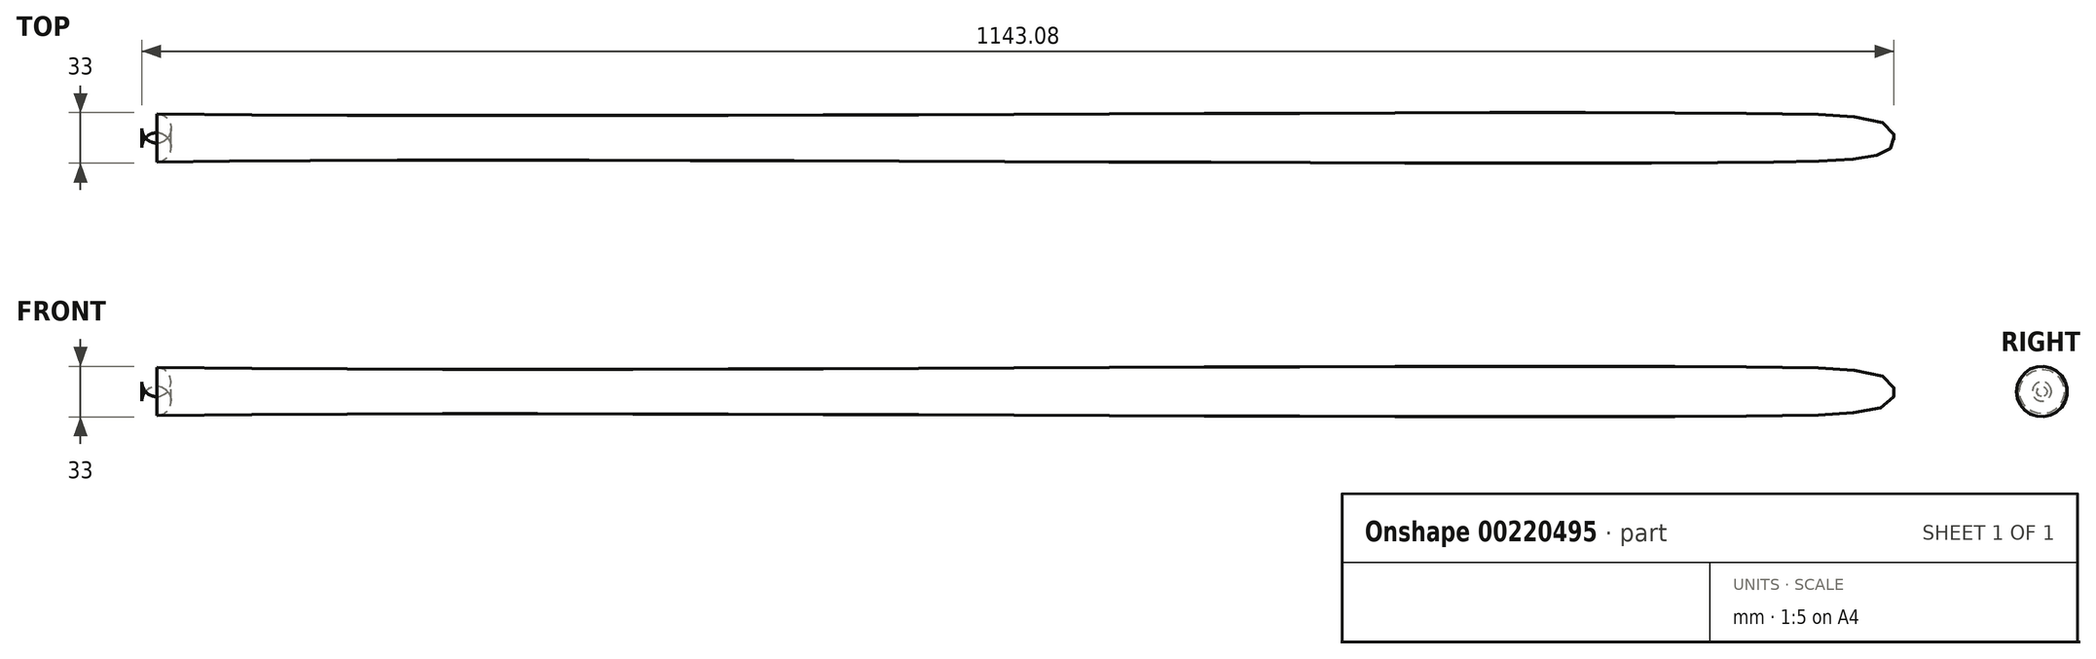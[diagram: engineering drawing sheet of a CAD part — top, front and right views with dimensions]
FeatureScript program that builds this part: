
annotation { "Feature Type Name" : "Feature", "Feature Type Description" : "" }
export const myFeature = defineFeature(function(context is Context, id is Id, definition is map)
    precondition{}
    {
        {
            var Q0;
            Q0=qCreatedBy(makeId("Top.planeOp"),FACE);
            var sketch = newSketch(context, id + "F0", { "sketchPlane" : qUnion([Q0])});
            skLineSegment(sketch, "E0", {"start": v(-571.5, 0) * mm, "end": v(571.5, 0) * mm});
            skLineSegment(sketch, "E1", {"start": v(-571.5, 0) * mm, "end": v(-571.5, -15.88) * mm});
            skFitSpline(sketch, "E2", {"points": [v(-571.5, -15.88) * mm, v(493.28, -15.87) * mm, v(571.5, 0) * mm], "startDerivative": vector(1003.6, 15.39) * mm, "endDerivative": vector(-23.38, 192.15) * mm});
            skSolve(sketch);
        }
        {
            var Q0;
            Q0=makeQuery(id+"F0.imprint","IMPRINT",FACE,{"disambiguationData":[TD([[makeQuery(id+"F0.imprint","IMPRINT",EDGE,{"derivedFrom":sQuery(id+"F0.wireOp",EDGE,"E0")}),-1.0]])]});
            var Q1;
            Q1=sQuery(id+"F0.wireOp",EDGE,"E0");
            revolve(context, id + "F1", {"entities" : qUnion([Q0]), "axis" : qUnion([Q1]), "revolveType" : RevolveType.FULL});
        }
        {
            var Q0;
            Q0=makeQuery(id+"F1.opRevolve","SWEPT_EDGE",EDGE,{"disambiguationData":[OSD([sQuery(id+"F0.wireOp",EDGE,"E1"),sQuery(id+"F0.wireOp",EDGE,"E2")])]});
            fillet(context, id + "F2", {"entities" : qUnion([Q0]), "radius" : 9.52 * mm, "tangentPropagation" : true, "allowEdgeOverflow" : false});
        }
    });
